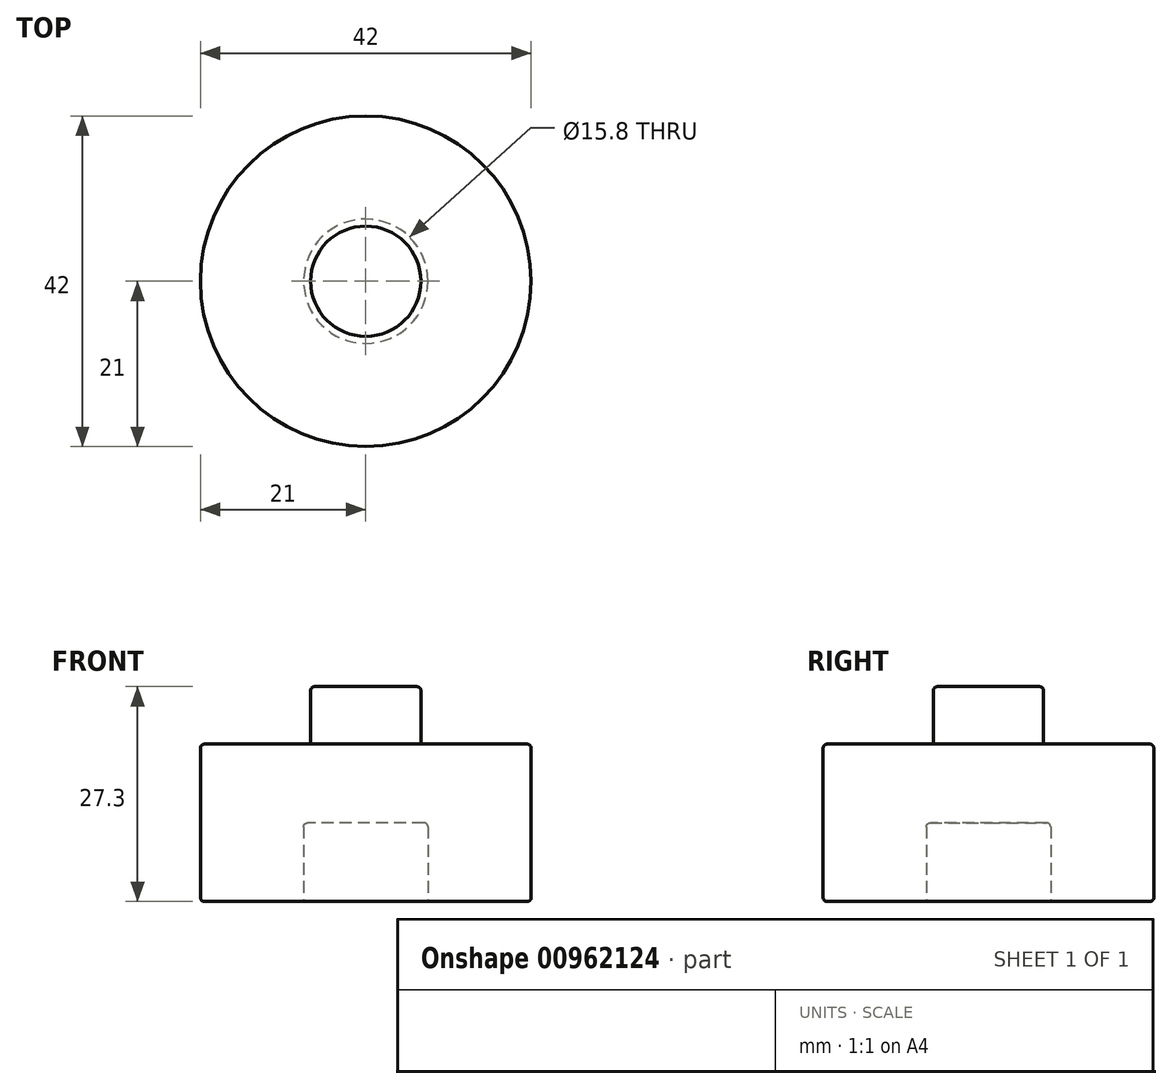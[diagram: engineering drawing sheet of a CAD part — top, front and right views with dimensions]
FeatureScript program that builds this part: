
annotation { "Feature Type Name" : "Feature", "Feature Type Description" : "" }
export const myFeature = defineFeature(function(context is Context, id is Id, definition is map)
    precondition{}
    {
        {
            assignVariable(context, id + "F0", {"variableType" : VariableType.LENGTH, "name" : "outer_circle_extrude", "lengthValue" : 20 * mm});
        }
        {
            assignVariable(context, id + "F1", {"variableType" : VariableType.LENGTH, "name" : "inner_circle_extrude", "lengthValue" : 10 * mm});
        }
        {
            assignVariable(context, id + "F2", {"variableType" : VariableType.LENGTH, "name" : "nipple_circle_extrude", "lengthValue" : 7.3 * mm});
        }
        {
            assignVariable(context, id + "F3", {"variableType" : VariableType.LENGTH, "name" : "fillet", "lengthValue" : 0.5 * mm});
        }
        {
            var Q0;
            Q0=qCreatedBy(makeId("Top.planeOp"),FACE);
            var sketch = newSketch(context, id + "F4", { "sketchPlane" : qUnion([Q0])});
            skCircle(sketch, "E0", {"center": v(0, 0) * mm, "radius": 21 * mm});
            skSolve(sketch);
        }
        {
            var Q0;
            Q0=makeQuery(id+"F4.imprint","IMPRINT",FACE,{"disambiguationData":[TD([[makeQuery(id+"F4.imprint","IMPRINT",EDGE,{"derivedFrom":sQuery(id+"F4.wireOp",EDGE,"E0")}),1.0]])]});
            extrude(context, id + "F5", {"entities" : qUnion([Q0]), "depth" : getVariable(context, 'outer_circle_extrude'), "offsetDistance" : 25 * mm});
        }
        {
            var Q0;
            Q0=qCreatedBy(makeId("Top.planeOp"),FACE);
            var sketch = newSketch(context, id + "F6", { "sketchPlane" : qUnion([Q0])});
            skCircle(sketch, "E1", {"center": v(0, 0) * mm, "radius": 7.9 * mm});
            skSolve(sketch);
        }
        {
            var Q0;
            Q0=makeQuery(id+"F6.imprint","IMPRINT",FACE,{"disambiguationData":[TD([[makeQuery(id+"F6.imprint","IMPRINT",EDGE,{"derivedFrom":sQuery(id+"F6.wireOp",EDGE,"E1")}),1.0]])]});
            extrude(context, id + "F7", {"entities" : qUnion([Q0]), "operationType" : NewBodyOperationType.REMOVE, "depth" : getVariable(context, 'inner_circle_extrude'), "offsetDistance" : 25 * mm});
        }
        {
            var Q0;
            Q0=makeQuery(id+"F5.opExtrude","CAP_FACE",FACE,{"disambiguationData":[OSD([sQuery(id+"F4.wireOp",EDGE,"E0")])],"isStart":false});
            var sketch = newSketch(context, id + "F8", { "sketchPlane" : qUnion([Q0])});
            skCircle(sketch, "E2", {"center": v(0, 0) * mm, "radius": 7 * mm});
            skSolve(sketch);
        }
        {
            var Q0;
            Q0=makeQuery(id+"F8.imprint","IMPRINT",FACE,{"disambiguationData":[TD([[makeQuery(id+"F8.imprint","IMPRINT",EDGE,{"derivedFrom":sQuery(id+"F8.wireOp",EDGE,"E2")}),1.0]])]});
            extrude(context, id + "F9", {"entities" : qUnion([Q0]), "operationType" : NewBodyOperationType.ADD, "depth" : getVariable(context, 'nipple_circle_extrude'), "offsetDistance" : 25 * mm});
        }
        {
            var Q0;
            Q0=makeQuery(id+"F9.opExtrude","CAP_EDGE",EDGE,{"disambiguationData":[OSD([sQuery(id+"F8.wireOp",EDGE,"E2")])],"isStart":false});
            var Q1;
            Q1=makeQuery(id+"F5.opExtrude","CAP_EDGE",EDGE,{"disambiguationData":[OSD([sQuery(id+"F4.wireOp",EDGE,"E0")])],"isStart":false});
            var Q2;
            Q2=makeQuery(id+"F5.opExtrude","CAP_EDGE",EDGE,{"disambiguationData":[OSD([sQuery(id+"F4.wireOp",EDGE,"E0")])],"isStart":true});
            var Q3;
            Q3=makeQuery(id+"F7.boolean.opBoolean","COPY",EDGE,{"derivedFrom":makeQuery(id+"F7.opExtrude","CAP_EDGE",EDGE,{"disambiguationData":[OSD([sQuery(id+"F6.wireOp",EDGE,"E1")])],"isStart":true})});
            var Q4;
            Q4=makeQuery(id+"F7.boolean.opBoolean","COPY",FACE,{"derivedFrom":makeQuery(id+"F7.opExtrude","CAP_FACE",FACE,{"disambiguationData":[OSD([sQuery(id+"F6.wireOp",EDGE,"E1")])],"isStart":false})});
            fillet(context, id + "F10", {"entities" : qUnion([Q0, Q1, Q2, Q3, Q4]), "radius" : getVariable(context, 'fillet'), "tangentPropagation" : true, "allowEdgeOverflow" : false});
        }
    });
